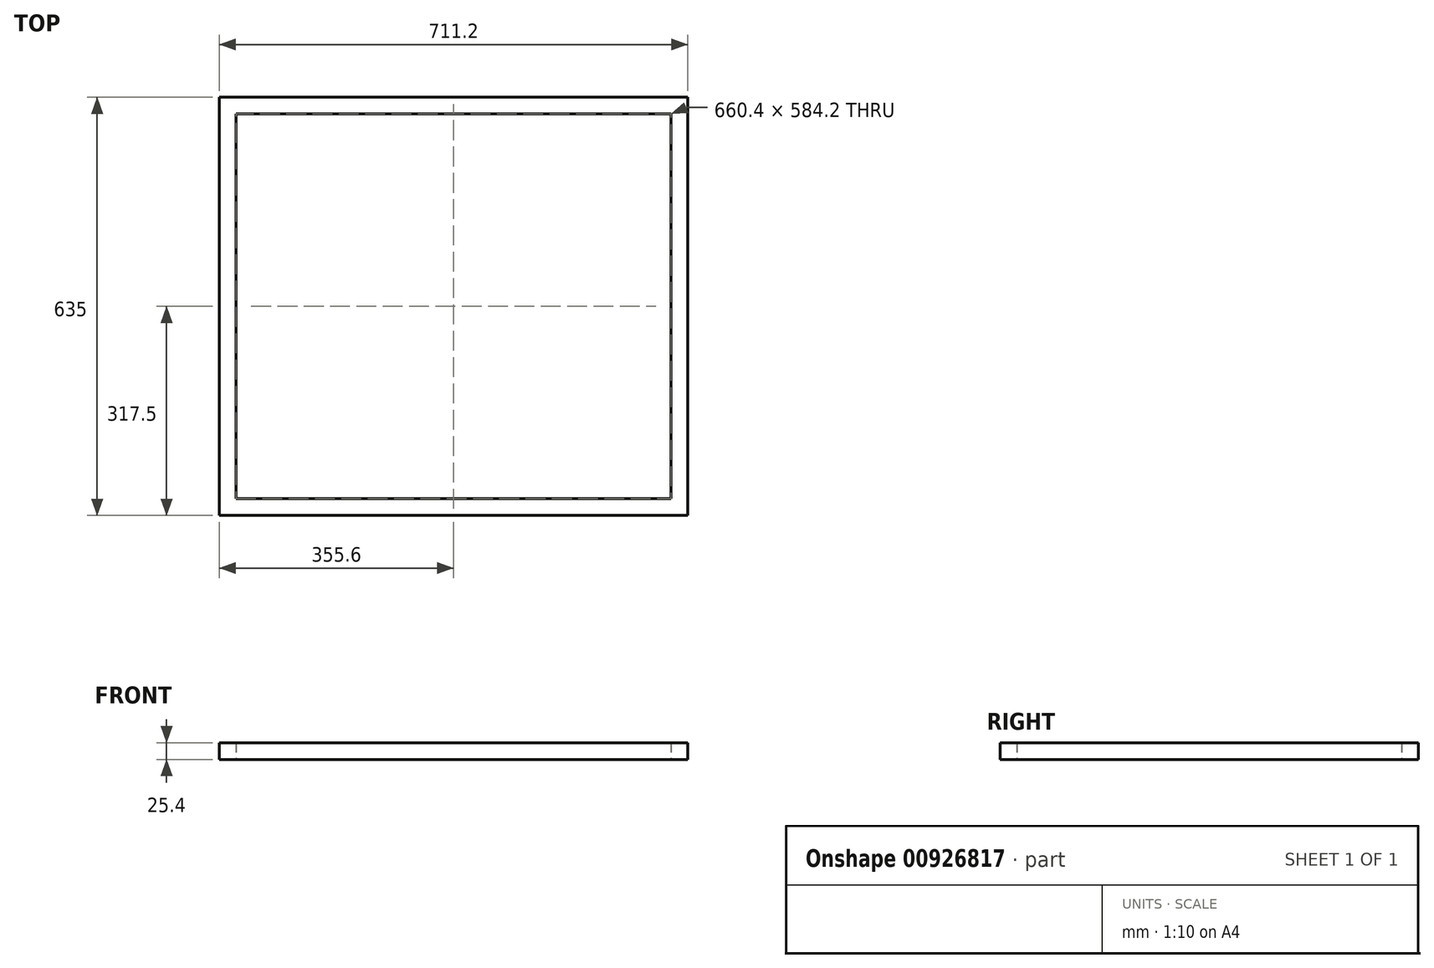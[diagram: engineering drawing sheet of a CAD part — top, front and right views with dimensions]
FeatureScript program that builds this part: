
annotation { "Feature Type Name" : "Feature", "Feature Type Description" : "" }
export const myFeature = defineFeature(function(context is Context, id is Id, definition is map)
    precondition{}
    {
        {
            var Q0;
            Q0=qCreatedBy(makeId("Top.planeOp"),FACE);
            var sketch = newSketch(context, id + "F0", { "sketchPlane" : qUnion([Q0])});
            skLineSegment(sketch, "E0.bottom", {"start": v(-330.2, 292.1) * mm, "end": v(330.2, 292.1) * mm});
            skLineSegment(sketch, "E0.top", {"start": v(-330.2, -292.1) * mm, "end": v(330.2, -292.1) * mm});
            skLineSegment(sketch, "E0.left", {"start": v(-330.2, 292.1) * mm, "end": v(-330.2, -292.1) * mm});
            skLineSegment(sketch, "E0.right", {"start": v(330.2, 292.1) * mm, "end": v(330.2, -292.1) * mm});
            skSolve(sketch);
        }
        {
            var Q0;
            Q0=qCreatedBy(makeId("Front.planeOp"),FACE);
            var sketch = newSketch(context, id + "F1", { "sketchPlane" : qUnion([Q0])});
            skLineSegment(sketch, "E1.bottom", {"start": v(-355.6, 12.7) * mm, "end": v(-330.2, 12.7) * mm});
            skLineSegment(sketch, "E1.top", {"start": v(-355.6, -12.7) * mm, "end": v(-330.2, -12.7) * mm});
            skLineSegment(sketch, "E1.left", {"start": v(-355.6, 12.7) * mm, "end": v(-355.6, -12.7) * mm});
            skLineSegment(sketch, "E1.right", {"start": v(-330.2, 12.7) * mm, "end": v(-330.2, -12.7) * mm});
            skSolve(sketch);
        }
        {
            var Q0;
            Q0=makeQuery(id+"F1.imprint","IMPRINT",FACE,{"disambiguationData":[TD([[makeQuery(id+"F1.imprint","IMPRINT",EDGE,{"derivedFrom":sQuery(id+"F1.wireOp",EDGE,"E1.bottom")}),-1.0]])]});
            var Q1;
            Q1=sQuery(id+"F0.wireOp",EDGE,"E0.left");
            var Q2;
            Q2=sQuery(id+"F0.wireOp",EDGE,"E0.bottom");
            var Q3;
            Q3=sQuery(id+"F0.wireOp",EDGE,"E0.right");
            var Q4;
            Q4=sQuery(id+"F0.wireOp",EDGE,"E0.top");
            sweep(context, id + "F2", {"profiles" : qUnion([Q0]), "path" : qUnion([Q1, Q2, Q3, Q4])});
        }
    });
